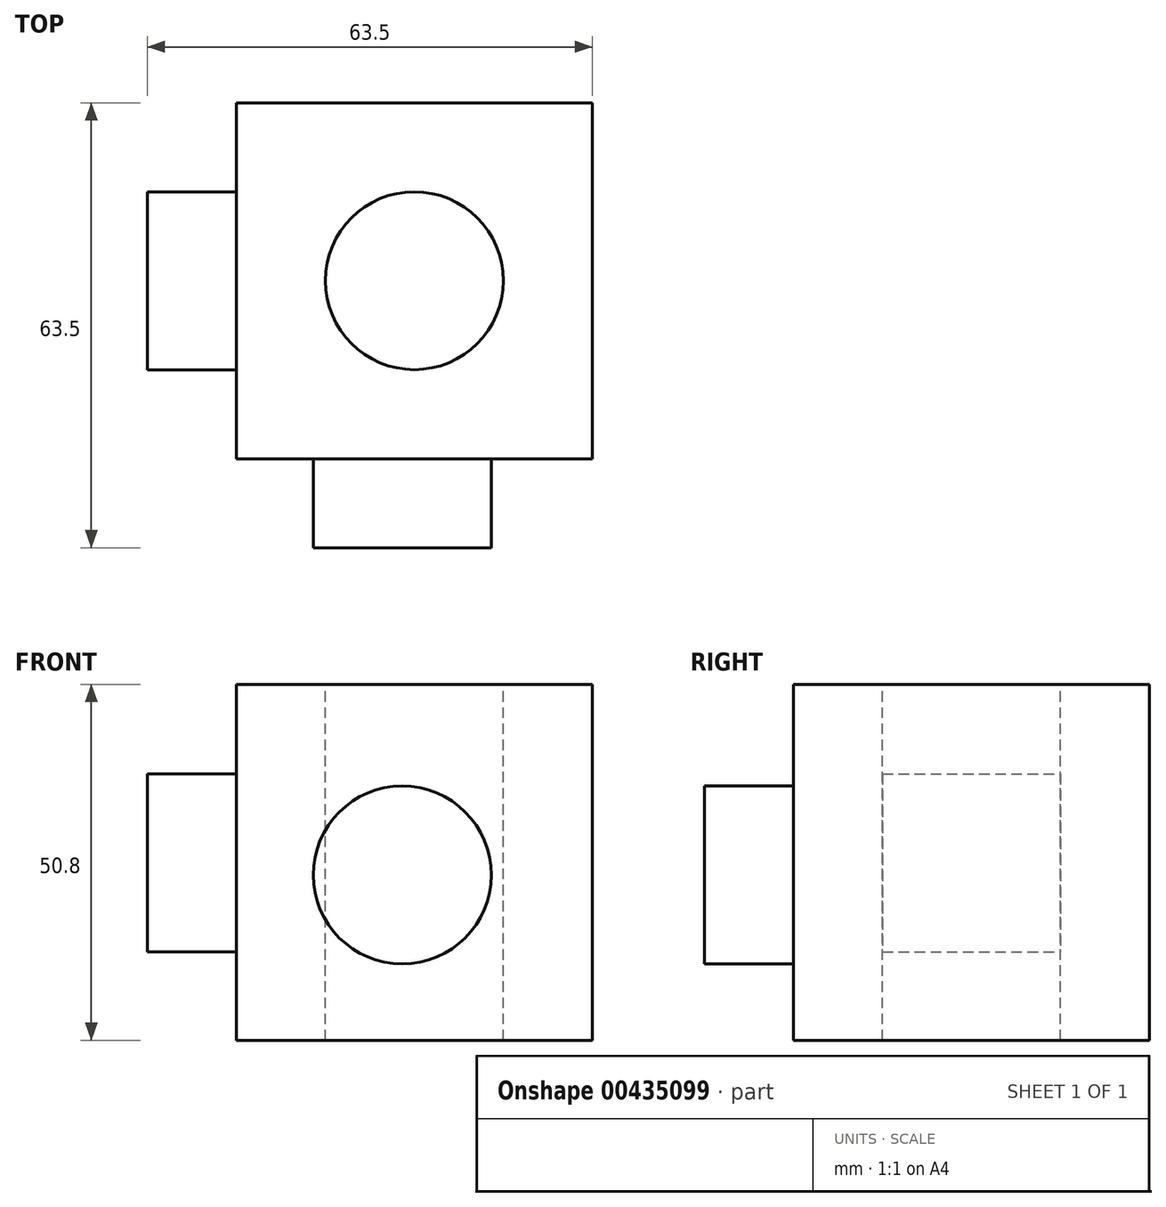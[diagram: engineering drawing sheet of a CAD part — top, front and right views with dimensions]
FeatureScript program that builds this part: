
annotation { "Feature Type Name" : "Feature", "Feature Type Description" : "" }
export const myFeature = defineFeature(function(context is Context, id is Id, definition is map)
    precondition{}
    {
        {
            var Q0;
            Q0=qCreatedBy(makeId("Front.planeOp"),FACE);
            var sketch = newSketch(context, id + "F0", { "sketchPlane" : qUnion([Q0])});
            skLineSegment(sketch, "E0", {"start": v(0, 0) * mm, "end": v(-50.8, 0) * mm});
            skLineSegment(sketch, "E1", {"start": v(-50.8, 0) * mm, "end": v(-50.8, 50.8) * mm});
            skLineSegment(sketch, "E2", {"start": v(-50.8, 50.8) * mm, "end": v(0, 50.8) * mm});
            skLineSegment(sketch, "E3", {"start": v(0, 50.8) * mm, "end": v(0, 0) * mm});
            skSolve(sketch);
        }
        {
            var Q0;
            Q0=makeQuery(id+"F0.imprint","IMPRINT",FACE,{"disambiguationData":[TD([[makeQuery(id+"F0.imprint","IMPRINT",EDGE,{"derivedFrom":sQuery(id+"F0.wireOp",EDGE,"E0")}),-1.0]])]});
            extrude(context, id + "F1", {"entities" : qUnion([Q0]), "depth" : 50.8 * mm});
        }
        {
            var Q0;
            Q0=makeQuery(id+"F1.opExtrude","CAP_FACE",FACE,{"disambiguationData":[OSD([sQuery(id+"F0.wireOp",EDGE,"E0"),sQuery(id+"F0.wireOp",EDGE,"E1"),sQuery(id+"F0.wireOp",EDGE,"E2"),sQuery(id+"F0.wireOp",EDGE,"E3")])],"isStart":false});
            var sketch = newSketch(context, id + "F2", { "sketchPlane" : qUnion([Q0])});
            skCircle(sketch, "E4", {"center": v(-27.13, 23.6) * mm, "radius": 12.7 * mm});
            skSolve(sketch);
        }
        {
            var Q0;
            Q0=makeQuery(id+"F2.imprint","IMPRINT",FACE,{"disambiguationData":[TD([[makeQuery(id+"F2.imprint","IMPRINT",EDGE,{"derivedFrom":sQuery(id+"F2.wireOp",EDGE,"E4")}),1.0]])]});
            extrude(context, id + "F3", {"entities" : qUnion([Q0]), "operationType" : NewBodyOperationType.ADD, "depth" : 12.7 * mm});
        }
        {
            var Q0;
            Q0=makeQuery(id+"F1.opExtrude","SWEPT_FACE",FACE,{"disambiguationData":[OSD([sQuery(id+"F0.wireOp",EDGE,"E1")])]});
            var sketch = newSketch(context, id + "F4", { "sketchPlane" : qUnion([Q0])});
            skLineSegment(sketch, "E5.bottom", {"start": v(38.1, 37.98) * mm, "end": v(12.7, 37.98) * mm});
            skLineSegment(sketch, "E5.top", {"start": v(38.1, 12.58) * mm, "end": v(12.7, 12.58) * mm});
            skLineSegment(sketch, "E5.left", {"start": v(38.1, 37.98) * mm, "end": v(38.1, 12.58) * mm});
            skLineSegment(sketch, "E5.right", {"start": v(12.7, 37.98) * mm, "end": v(12.7, 12.58) * mm});
            skSolve(sketch);
        }
        {
            var Q0;
            Q0=makeQuery(id+"F4.imprint","IMPRINT",FACE,{"disambiguationData":[TD([[makeQuery(id+"F4.imprint","IMPRINT",EDGE,{"derivedFrom":sQuery(id+"F4.wireOp",EDGE,"E5.bottom")}),1.0]])]});
            extrude(context, id + "F5", {"entities" : qUnion([Q0]), "operationType" : NewBodyOperationType.ADD, "depth" : 12.7 * mm});
        }
        {
            var Q0;
            Q0=makeQuery(id+"F1.opExtrude","SWEPT_FACE",FACE,{"disambiguationData":[OSD([sQuery(id+"F0.wireOp",EDGE,"E2")])]});
            var sketch = newSketch(context, id + "F6", { "sketchPlane" : qUnion([Q0])});
            skCircle(sketch, "E6", {"center": v(-25.4, -25.4) * mm, "radius": 12.7 * mm});
            skSolve(sketch);
        }
        {
            var Q0;
            Q0=makeQuery(id+"F6.imprint","IMPRINT",FACE,{"disambiguationData":[TD([[makeQuery(id+"F6.imprint","IMPRINT",EDGE,{"derivedFrom":sQuery(id+"F6.wireOp",EDGE,"E6")}),1.0]])]});
            extrude(context, id + "F7", {"entities" : qUnion([Q0]), "operationType" : NewBodyOperationType.REMOVE, "oppositeDirection" : true, "depth" : 50.8 * mm});
        }
    });
